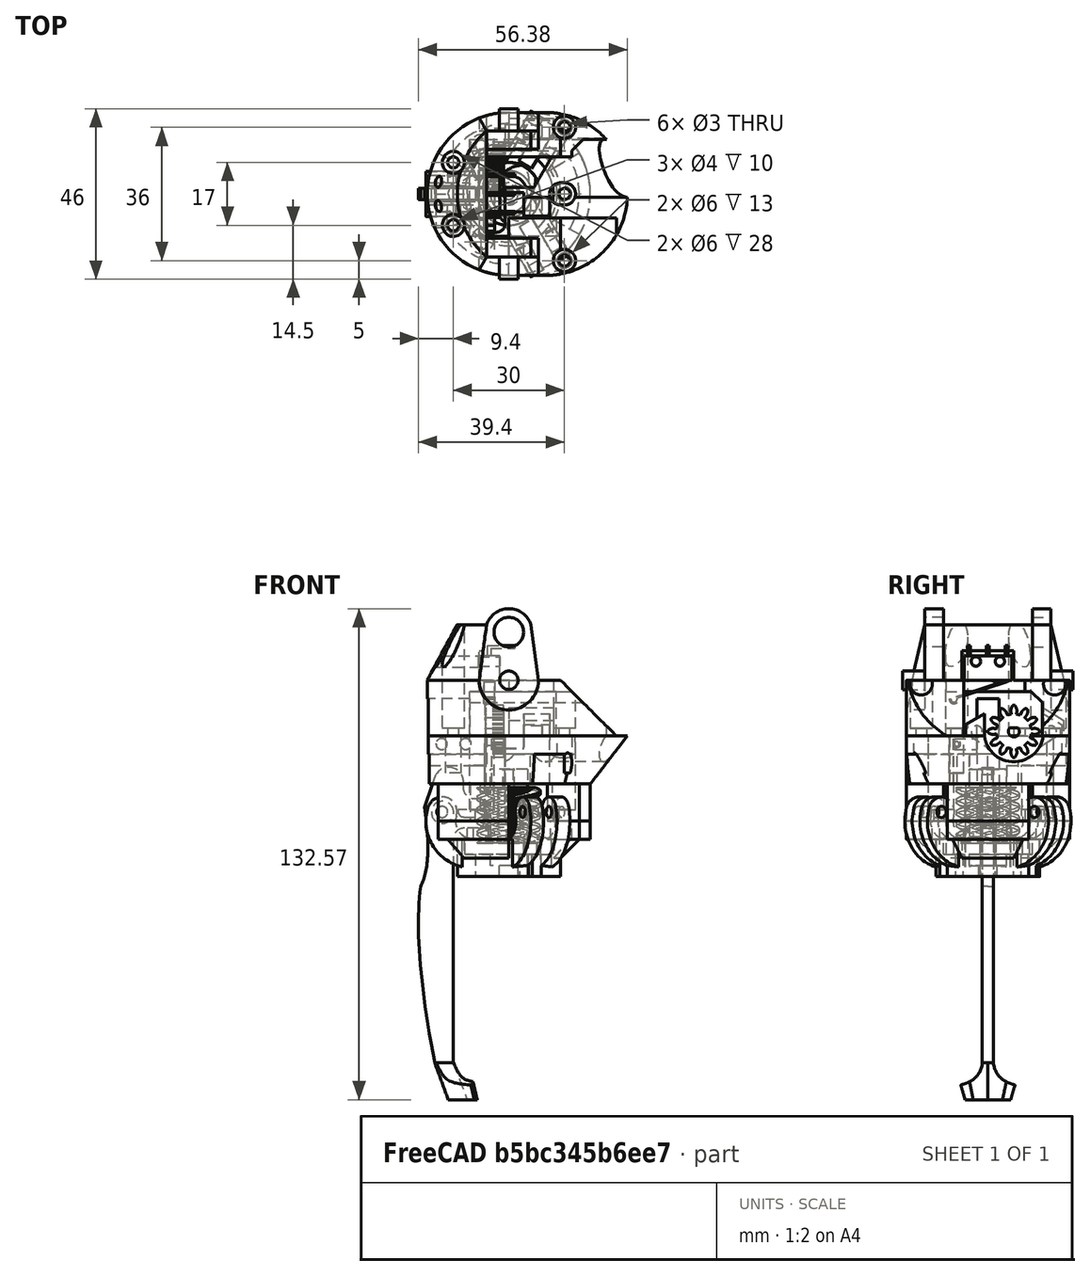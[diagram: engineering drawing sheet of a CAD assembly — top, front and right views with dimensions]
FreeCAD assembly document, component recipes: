
FREECAD ASSEMBLY — COMPONENT RECIPES ("GripperHolder")

This assembly document has 11 components, labeled P0..P10 below (a component is one placed body or linked part). 6 of them carry a construction recipe — the FreeCAD feature program that regenerates the part from scratch, quoted from this document or its linked companion documents; the rest are supplied as boundary geometry only. No exploded tour is included for this assembly.
COMPONENT P0 — recipe-attached ("GripperFinger", modeled in this document).
Construction recipe (the document's own serialized feature program — sketch geometry with constraints, then the solid features built on it; lengths are millimeters unless a unit is written):

FEATURE [Sketcher::SketchObject] Sketch014
  ArcFitTolerance = 1e-06
  AttachmentSupport = -> [XZ_Plane002]
  FullyConstrained = false
  MakeInternals = false
  MapMode = 5
  Placement = pos=(0,0,0) rot=(1,0,0;1.5708rad)
  sketch-geometry (24):
    g0: Circle [constr] CenterX=-20.7594 CenterY=-8.82234 CenterZ=0 NormalX=0 NormalY=0 NormalZ=1 AngleXU=0 Radius=1
    g1: Circle [constr] CenterX=-18.5613 CenterY=-24.1579 CenterZ=0 NormalX=0 NormalY=0 NormalZ=1 AngleXU=0 Radius=1
    g2: Circle [constr] CenterX=-21.8082 CenterY=-30.1322 CenterZ=0 NormalX=0 NormalY=0 NormalZ=1 AngleXU=0 Radius=1
    g3: BSplineCurve PolesCount=3 KnotsCount=2 Degree=2 IsPeriodic=0
    g4: GeomPoint [constr] X=-20.7594 Y=-8.82234 Z=0
    g5: GeomPoint [constr] X=-21.8082 Y=-30.1322 Z=0
    g6: Circle [constr] CenterX=-21.8082 CenterY=-30.1322 CenterZ=0 NormalX=0 NormalY=0 NormalZ=1 AngleXU=0 Radius=1
    g7: Circle [constr] CenterX=-24.0161 CenterY=-46.7563 CenterZ=0 NormalX=0 NormalY=0 NormalZ=1 AngleXU=0 Radius=1
    g8: Circle [constr] CenterX=-18 CenterY=-77.753 CenterZ=0 NormalX=0 NormalY=0 NormalZ=1 AngleXU=0 Radius=1
    g9: BSplineCurve PolesCount=3 KnotsCount=2 Degree=2 IsPeriodic=0
    g10: GeomPoint [constr] X=-21.8082 Y=-30.1322 Z=0
    g11: GeomPoint [constr] X=-18 Y=-77.753 Z=0
    g12: LineSegment StartX=-18 StartY=-77.753 StartZ=0 EndX=-13 EndY=-77.753 EndZ=0
    g13: LineSegment StartX=-20.7594 StartY=-8.82234 StartZ=0 EndX=-17.7673 EndY=-0.0858362 EndZ=0
    g14: ArcOfCircle CenterX=-14.2357 CenterY=-1.99234 CenterZ=0 NormalX=0 NormalY=0 NormalZ=1 AngleXU=0 Radius=4.01341 StartAngle=5.91393 EndAngle=8.92978
    g15: LineSegment StartX=-11.4259 StartY=-6.40926 StartZ=0 EndX=-10.4928 EndY=-3.44087 EndZ=0
    g16: LineSegment StartX=-13 StartY=-14.4093 StartZ=0 EndX=-13 EndY=-77.753 EndZ=0
    g17: LineSegment StartX=-11.4259 StartY=-6.40926 StartZ=0 EndX=-4.71716 EndY=-6.40926 EndZ=0
    g18: LineSegment StartX=-4.71716 StartY=-6.40926 StartZ=0 EndX=-4.71716 EndY=-9.40926 EndZ=0
    g19: LineSegment StartX=-4.71716 StartY=-9.40926 StartZ=0 EndX=-11.7172 EndY=-9.40926 EndZ=0
    g20: LineSegment StartX=-11.7172 StartY=-9.40926 StartZ=0 EndX=-11.7172 EndY=-11.4093 EndZ=0
    g21: LineSegment StartX=-11.7172 StartY=-11.4093 StartZ=0 EndX=-4.71716 EndY=-11.4093 EndZ=0
    g22: LineSegment StartX=-4.71716 StartY=-11.4093 StartZ=0 EndX=-4.71716 EndY=-14.4093 EndZ=0
    g23: LineSegment StartX=-4.71716 StartY=-14.4093 StartZ=0 EndX=-13 EndY=-14.4093 EndZ=0
  constraints (45):
    c: Weight(g0) = 1
    c: Equal(g0,g1)
    c: Equal(g0,g2)
    c: InternalAlignment(g0,g3)
    c: InternalAlignment(g1,g3)
    c: InternalAlignment(g2,g3)
    c: InternalAlignment(g4,g3)
    c: InternalAlignment(g5,g3)
    c: Weight(g6) = 1
    c: Equal(g6,g7)
    c: Equal(g6,g8)
    c: InternalAlignment(g6,g9)
    c: InternalAlignment(g7,g9)
    c: InternalAlignment(g8,g9)
    c: InternalAlignment(g10,g9)
    c: InternalAlignment(g11,g9)
    c: Coincident(g2,g6)
    c: Horizontal(g12,g8)
    c: Coincident(g12,g9)
    c: DistanceX(g12,g12) = 5
    c: Coincident(g13,g3)
    c: Coincident(g14,g13)
    c: Horizontal(g17)
    c: Coincident(g17,g18)
    c: Vertical(g18)
    c: Coincident(g18,g19)
    c: Horizontal(g19)
    c: Coincident(g19,g20)
    c: Vertical(g20)
    c: Coincident(g20,g21)
    c: Horizontal(g21)
    c: Coincident(g21,g22)
    c: Vertical(g22)
    c: Distance(g18,g18) = 3
    c: DistanceY(g22,g22) = 3
    c: DistanceY(g20,g20) = 2
    c: Vertical(g16)
    c: Coincident(g15,g17)
    c: Horizontal(g23)
    c: Coincident(g23,g22)
    c: Coincident(g16,g23)
    c: Vertical(g19,g21)
    c: Coincident(g14,g15)
    c: Coincident(g12,g16)
    c: DistanceX(g19,g19) = 7
FEATURE [PartDesign::Pad] Pad003
  Direction = (0,-1,2e-16)
  Length = 1.5
  Length2 = 10
  Placement = pos=(0,0,0) rot=(1,0,0;1.5708rad)
  Profile = -> Sketch014
  ReferenceAxis = -> Sketch014 [N_Axis]
  Refine = true
  Suppressed = false
  Type = 0
FEATURE [Sketcher::SketchObject] Sketch015
  ArcFitTolerance = 1e-06
  AttachmentSupport = -> [XZ_Plane002]
  FullyConstrained = false
  MakeInternals = false
  MapMode = 5
  Placement = pos=(0,0,0) rot=(1,0,0;1.5708rad)
  sketch-geometry (1):
    g0: Circle CenterX=-15.9022 CenterY=-10.1693 CenterZ=0 NormalX=0 NormalY=0 NormalZ=1 AngleXU=0 Radius=3
  constraints (1):
    c: Diameter(g0) = 6
FEATURE [PartDesign::Pocket] Pocket010
  BaseFeature = -> Pad003
  Direction = (0,1,-2e-16)
  Length = 5
  Length2 = 5
  Placement = pos=(0,0,0) rot=(1,0,0;1.5708rad)
  Profile = -> Sketch015
  ReferenceAxis = -> Sketch015 [N_Axis]
  Refine = true
  Reversed = true
  Suppressed = false
  Type = 0
FEATURE [Sketcher::SketchObject] Sketch016
  ArcFitTolerance = 1e-06
  AttachmentSupport = -> [Pocket010]
  FullyConstrained = false
  MakeInternals = false
  MapMode = 5
  Placement = pos=(0,-3.42e-14,-77.753) rot=(1,0,0;3.14159rad)
  sketch-geometry (10):
    g0: Circle [constr] CenterX=-13 CenterY=0 CenterZ=0 NormalX=0 NormalY=0 NormalZ=1 AngleXU=0 Radius=1
    g1: Circle [constr] CenterX=-13.004 CenterY=4.51884 CenterZ=0 NormalX=0 NormalY=0 NormalZ=1 AngleXU=0 Radius=1
    g2: Circle [constr] CenterX=-8.86046 CenterY=6.03618 CenterZ=0 NormalX=0 NormalY=0 NormalZ=1 AngleXU=0 Radius=1
    g3: BSplineCurve PolesCount=3 KnotsCount=2 Degree=2 IsPeriodic=0
    g4: Circle [constr] CenterX=-18 CenterY=0 CenterZ=0 NormalX=0 NormalY=0 NormalZ=1 AngleXU=0 Radius=1
    g5: Circle [constr] CenterX=-16.3304 CenterY=6.85321 CenterZ=0 NormalX=0 NormalY=0 NormalZ=1 AngleXU=0 Radius=1
    g6: Circle [constr] CenterX=-9.56077 CenterY=9.07086 CenterZ=0 NormalX=0 NormalY=0 NormalZ=1 AngleXU=0 Radius=1
    g7: BSplineCurve PolesCount=3 KnotsCount=2 Degree=2 IsPeriodic=0
    g8: LineSegment StartX=-9.56077 StartY=9.07086 StartZ=0 EndX=-8.86046 EndY=6.03618 EndZ=0
    g9: LineSegment StartX=-13 StartY=0 StartZ=0 EndX=-18 EndY=0 EndZ=0
  constraints (16):
    c: Weight(g0) = 1
    c: Equal(g0,g1)
    c: Equal(g0,g2)
    c: InternalAlignment(g0,g3)
    c: InternalAlignment(g1,g3)
    c: InternalAlignment(g2,g3)
    c: Weight(g4) = 1
    c: Equal(g4,g5)
    c: Equal(g4,g6)
    c: InternalAlignment(g4,g7)
    c: InternalAlignment(g5,g7)
    c: InternalAlignment(g6,g7)
    c: Coincident(g8,g7)
    c: Coincident(g8,g3)
    c: Coincident(g9,g7)
    c: Coincident(g9,g3)
FEATURE [Sketcher::SketchObject] Sketch017
  ArcFitTolerance = 1e-06
  AttachmentOffset = pos=(0,0,10) rot=(0,0,1;0rad)
  AttachmentSupport = -> [Pocket010]
  FullyConstrained = false
  MakeInternals = false
  MapMode = 5
  Placement = pos=(0,-3.42e-14,-87.753) rot=(1,0,0;3.14159rad)
  sketch-geometry (8):
    g0: Circle [constr] CenterX=-13.474 CenterY=5.13044 CenterZ=0 NormalX=0 NormalY=0 NormalZ=1 AngleXU=0 Radius=1
    g1: Circle [constr] CenterX=-7.36415 CenterY=6.15312 CenterZ=0 NormalX=0 NormalY=0 NormalZ=1 AngleXU=0 Radius=1
    g2: BSplineCurve PolesCount=3 KnotsCount=2 Degree=2 IsPeriodic=0
    g3: Circle [constr] CenterX=-9.38329 CenterY=2.79664 CenterZ=0 NormalX=0 NormalY=0 NormalZ=1 AngleXU=0 Radius=1
    g4: Circle [constr] CenterX=-6.52503 CenterY=3.95043 CenterZ=0 NormalX=0 NormalY=0 NormalZ=1 AngleXU=0 Radius=1
    g5: BSplineCurve PolesCount=3 KnotsCount=2 Degree=2 IsPeriodic=0
    g6: LineSegment StartX=-7.36415 StartY=6.15312 StartZ=0 EndX=-6.52503 EndY=3.95043 EndZ=0
    g7: LineSegment StartX=-14.3465 StartY=0 StartZ=0 EndX=-9.25279 EndY=0 EndZ=0
  constraints (10):
    c: InternalAlignment(g0,g2)
    c: InternalAlignment(g1,g2)
    c: InternalAlignment(g3,g5)
    c: InternalAlignment(g4,g5)
    c: Coincident(g6,g2)
    c: Coincident(g6,g5)
    c: Coincident(g7,g2)
    c: Horizontal(g7)
    c: Coincident(g5,g7)
    c: Horizontal(g5,g-1)
FEATURE [PartDesign::AdditiveLoft] AdditiveLoft002
  BaseFeature = -> Pocket010
  Closed = true
  Placement = pos=(0,0,0) rot=(1,0,0;1.5708rad)
  Profile = -> Sketch016
  Refine = true
  Ruled = true
  Sections = -> [Sketch017]
  Suppressed = false
FEATURE [Sketcher::SketchObject] Sketch018
  ArcFitTolerance = 1e-06
  AttachmentSupport = -> [YZ_Plane002]
  ExternalGeometry = -> [AdditiveLoft002]
  FullyConstrained = false
  MakeInternals = false
  MapMode = 5
  Placement = pos=(0,0,0) rot=(0.57735,0.57735,0.57735;2.0944rad)
  sketch-geometry (9):
    g0: Circle [constr] CenterX=-25.4284 CenterY=-84.2513 CenterZ=0 NormalX=0 NormalY=0 NormalZ=1 AngleXU=0 Radius=1
    g1: Circle [constr] CenterX=-2.16974 CenterY=-84.4568 CenterZ=0 NormalX=0 NormalY=0 NormalZ=1 AngleXU=0 Radius=1
    g2: Circle [constr] CenterX=-1.5 CenterY=-77.753 CenterZ=0 NormalX=0 NormalY=0 NormalZ=1 AngleXU=0 Radius=1
    g3: BSplineCurve PolesCount=3 KnotsCount=2 Degree=2 IsPeriodic=0
    g4: GeomPoint [constr] X=-12.8183 Y=-84.2513 Z=0
    g5: GeomPoint [constr] X=-1.5 Y=-77.753 Z=0
    g6: LineSegment StartX=-14.8386 StartY=-84.2513 StartZ=0 EndX=-14.8386 EndY=-77.2874 EndZ=0
    g7: LineSegment StartX=-14.8386 StartY=-77.2874 StartZ=0 EndX=-1.5 EndY=-77.753 EndZ=0
    g8: LineSegment StartX=-14.8386 StartY=-84.2513 StartZ=0 EndX=-12.8183 EndY=-84.2513 EndZ=0
  constraints (14):
    c: Weight(g0) = 1
    c: Equal(g0,g1)
    c: Equal(g0,g2)
    c: InternalAlignment(g1,g3)
    c: InternalAlignment(g2,g3)
    c: InternalAlignment(g4,g3)
    c: InternalAlignment(g5,g3)
    c: Vertical(g6)
    c: Coincident(g6,g7)
    c: Coincident(g7,g3)
    c: Coincident(g6,g8)
    c: Coincident(g8,g3)
    c: Horizontal(g8)
    c: Horizontal(g3,g0)
FEATURE [PartDesign::Pocket] Pocket005
  BaseFeature = -> AdditiveLoft002
  Direction = (-1,0,0)
  Length = 5
  Length2 = 5
  Placement = pos=(0,0,0) rot=(1,0,0;1.5708rad)
  Profile = -> Sketch018
  ReferenceAxis = -> Sketch018 [N_Axis]
  Refine = true
  Suppressed = false
  Type = 1
FEATURE [PartDesign::Mirrored] Mirrored001
  BaseFeature = -> Pocket005
  MirrorPlane = -> XZ_Plane002
  Placement = pos=(0,0,0) rot=(1,0,0;1.5708rad)
  Refine = true
  Suppressed = false
  TransformMode = 1
FEATURE [PartDesign::Fillet] Fillet
  Base = -> Mirrored001 [Edge70,Edge68]
  BaseFeature = -> Mirrored001
  Placement = pos=(0,0,0) rot=(1,0,0;1.5708rad)
  Radius = 3
  Refine = true
  SupportTransform = false
  Suppressed = false
  UseAllEdges = false
FEATURE [PartDesign::Fillet] Fillet001
  Base = -> Fillet [Edge26,Edge49,Edge37]
  BaseFeature = -> Fillet
  Placement = pos=(0,0,0) rot=(1,0,0;1.5708rad)
  Radius = 1.5
  Refine = true
  SupportTransform = false
  Suppressed = false
  UseAllEdges = false
FEATURE [PartDesign::Body] Body002  label="GripperFinger"
  AllowCompound = false
  Group = -> [Sketch014,Pad003,Pocket010,Sketch015,Sketch016,Sketch017,AdditiveLoft002,Sketch018,Pocket005,Mirrored001,Fillet,Fillet001]
  Origin = -> Origin002
  Placement = pos=(-2,0,-10.5) rot=(0,0,1;0rad)
  Tip = -> Fillet001
COMPONENT P1 — recipe-attached ("GripperHolderBottom", modeled in this document).
Construction recipe (the document's own serialized feature program — sketch geometry with constraints, then the solid features built on it; lengths are millimeters unless a unit is written):

FEATURE [Sketcher::SketchObject] Sketch024
  ArcFitTolerance = 1e-06
  AttachmentSupport = -> [XY_Plane004]
  FullyConstrained = true
  MakeInternals = false
  MapMode = 5
  sketch-geometry (2):
    g0: Circle CenterX=0 CenterY=0 CenterZ=0 NormalX=0 NormalY=0 NormalZ=1 AngleXU=0 Radius=2.5
    g1: Circle CenterX=0 CenterY=0 CenterZ=0 NormalX=0 NormalY=0 NormalZ=1 AngleXU=0 Radius=14
  constraints (4):
    c: Coincident(g0,g-1)
    c: Coincident(g1,g0)
    c: Diameter(g1) = 28
    c: Diameter(g0) = 5
FEATURE [PartDesign::Pad] Pad006
  Direction = (0,0,1)
  Length = 10
  Length2 = 10
  Profile = -> Sketch024
  ReferenceAxis = -> Sketch024 [N_Axis]
  Refine = true
  Reversed = true
  Suppressed = false
  Type = 0
FEATURE [Sketcher::SketchObject] Sketch025
  ArcFitTolerance = 1e-06
  AttachmentOffset = pos=(0,0,2.1) rot=(0,0,1;0rad)
  AttachmentSupport = -> [XZ_Plane004]
  FullyConstrained = false
  MakeInternals = false
  MapMode = 5
  Placement = pos=(0,-2.1,5e-16) rot=(1,0,0;1.5708rad)
  sketch-geometry (4):
    g0: ArcOfCircle CenterX=-9.71119 CenterY=4.94669 CenterZ=0 NormalX=0 NormalY=0 NormalZ=1 AngleXU=0 Radius=12.6732 StartAngle=2.84277 EndAngle=4.68735
    g1: ArcOfCircle CenterX=-18 CenterY=7.5 CenterZ=0 NormalX=0 NormalY=0 NormalZ=1 AngleXU=0 Radius=4 StartAngle=5.98437 EndAngle=9.12596
    g2: ArcOfCircle CenterX=-9.92832 CenterY=-3.72375 CenterZ=0 NormalX=0 NormalY=0 NormalZ=1 AngleXU=0 Radius=4 StartAngle=4.68735 EndAngle=7.82894
    g3: ArcOfCircle CenterX=-9.71119 CenterY=4.94669 CenterZ=0 NormalX=0 NormalY=0 NormalZ=1 AngleXU=0 Radius=4.67316 StartAngle=2.84277 EndAngle=4.68735
  constraints (8):
    c: Coincident(g0,g3)
    c: Tangent(g3,g2) = 1.5708
    c: Tangent(g3,g1) = 1.5708
    c: Tangent(g0,g2) = -1.5708
    c: Tangent(g0,g1) = -1.5708
    c: Radius(g1) = 4
    c: DistanceY(g-1,g1) = 7.5
    c: DistanceX(g1,g-1) = 18
FEATURE [PartDesign::Pad] Pad007
  BaseFeature = -> Pad006
  Direction = (0,-1,2e-16)
  Length = 4
  Length2 = 10
  Profile = -> Sketch025
  ReferenceAxis = -> Sketch025 [N_Axis]
  Refine = true
  Suppressed = false
  Type = 0
FEATURE [Sketcher::SketchObject] Sketch026
  ArcFitTolerance = 1e-06
  AttachmentSupport = -> [Pad007]
  FullyConstrained = false
  MakeInternals = false
  MapMode = 5
  Placement = pos=(0,-6.1,1.3e-15) rot=(1,0,0;1.5708rad)
  sketch-geometry (1):
    g0: Circle CenterX=-17.9735 CenterY=7.44527 CenterZ=0 NormalX=0 NormalY=0 NormalZ=1 AngleXU=0 Radius=1.5
  constraints (1):
    c: Diameter(g0) = 3
FEATURE [PartDesign::Pocket] Pocket011
  BaseFeature = -> Pad007
  Direction = (0,1,-2e-16)
  Length = 5
  Length2 = 5
  Profile = -> Sketch026
  ReferenceAxis = -> Sketch026 [N_Axis]
  Refine = true
  Suppressed = false
  Type = 0
FEATURE [PartDesign::Mirrored] Mirrored003
  BaseFeature = -> Pocket011
  MirrorPlane = -> XZ_Plane004
  Originals = -> [Pocket011]
  Refine = true
  Suppressed = false
  TransformMode = 1
FEATURE [PartDesign::PolarPattern] PolarPattern001
  Angle = 360
  Axis = -> Z_Axis004
  BaseFeature = -> Mirrored003
  Mode = 0
  Occurrences = 3
  Offset = 120
  Originals = -> [Mirrored003]
  Refine = true
  Suppressed = false
  TransformMode = 1
FEATURE [Sketcher::SketchObject] Sketch027
  ArcFitTolerance = 1e-06
  AttachmentSupport = -> [PolarPattern001]
  FullyConstrained = false
  MakeInternals = false
  MapMode = 5
  sketch-geometry (4):
    g0: ArcOfCircle CenterX=0 CenterY=0 CenterZ=0 NormalX=0 NormalY=0 NormalZ=1 AngleXU=0 Radius=22 StartAngle=1.57083 EndAngle=2.61805
    g1: LineSegment StartX=-19.0531 StartY=10.999 StartZ=0 EndX=-11.2589 EndY=6.49899 EndZ=0
    g2: ArcOfCircle CenterX=0 CenterY=0 CenterZ=0 NormalX=0 NormalY=0 NormalZ=1 AngleXU=0 Radius=13 StartAngle=1.57085 EndAngle=2.61808
    g3: LineSegment StartX=-0.000708834 StartY=22 StartZ=0 EndX=-0.000708834 EndY=13 EndZ=0
  constraints (10):
    c: Coincident(g0,g-1)
    c: Coincident(g1,g0)
    c: Coincident(g1,g2)
    c: Coincident(g3,g0)
    c: Coincident(g3,g2)
    c: Angle(g1,g-1) = 0.523599
    c: Vertical(g3)
    c: Coincident(g0,g2)
    c: Radius(g0) = 22
    c: Radius(g2) = 13
FEATURE [PartDesign::Pad] Pad008
  BaseFeature = -> PolarPattern001
  Direction = (0,0,1)
  Length = 5
  Length2 = 10
  Profile = -> Sketch027
  ReferenceAxis = -> Sketch027 [N_Axis]
  Refine = true
  Suppressed = false
  Type = 0
FEATURE [PartDesign::PolarPattern] PolarPattern002
  Angle = 360
  Axis = -> Sketch027 [N_Axis]
  BaseFeature = -> Pad008
  Mode = 0
  Occurrences = 3
  Offset = 120
  Originals = -> [Pad008]
  Refine = true
  Suppressed = false
  TransformMode = 0
FEATURE [Sketcher::SketchObject] Sketch031
  ArcFitTolerance = 1e-06
  AttachmentSupport = -> [YZ_Plane004]
  FullyConstrained = true
  MakeInternals = false
  MapMode = 5
  Placement = pos=(0,0,0) rot=(0.57735,0.57735,0.57735;2.0944rad)
  sketch-geometry (4):
    g0: LineSegment StartX=3 StartY=22 StartZ=0 EndX=-3 EndY=22 EndZ=0
    g1: LineSegment StartX=-3 StartY=22 StartZ=0 EndX=-3 EndY=15 EndZ=0
    g2: LineSegment StartX=-3 StartY=15 StartZ=0 EndX=3 EndY=15 EndZ=0
    g3: LineSegment StartX=3 StartY=15 StartZ=0 EndX=3 EndY=22 EndZ=0
  constraints (12):
    c: Coincident(g0,g1)
    c: Coincident(g1,g2)
    c: Coincident(g2,g3)
    c: Coincident(g3,g0)
    c: Horizontal(g0)
    c: Horizontal(g2)
    c: Vertical(g1)
    c: Vertical(g3)
    c: Distance(g-1,g2) = 15
    c: Distance(g-2,g1) = 3
    c: Distance(g-2,g3) = 3
    c: DistanceY(g3,g3) = 7
FEATURE [PartDesign::Pocket] Pocket013
  BaseFeature = -> PolarPattern002
  Direction = (-1,0,0)
  Length = 5
  Length2 = 5
  Profile = -> Sketch031
  ReferenceAxis = -> Sketch031 [N_Axis]
  Refine = true
  Suppressed = false
  Type = 1
FEATURE [PartDesign::PolarPattern] PolarPattern005
  Angle = 360
  Axis = -> Z_Axis004
  BaseFeature = -> Pocket013
  Mode = 0
  Occurrences = 3
  Offset = 120
  Originals = -> [Pocket013]
  Refine = true
  Suppressed = false
  TransformMode = 0
FEATURE [PartDesign::Chamfer] Chamfer
  Angle = 45
  Base = -> PolarPattern005 [Edge60,Edge61,Edge67,Edge68,Edge53,Edge48]
  BaseFeature = -> PolarPattern005
  ChamferType = 0
  FlipDirection = false
  Refine = true
  Size = 5
  Size2 = 7
  SupportTransform = false
  Suppressed = false
  UseAllEdges = false
FEATURE [Sketcher::SketchObject] Sketch048
  ArcFitTolerance = 1e-06
  AttachmentSupport = -> [Chamfer]
  FullyConstrained = true
  MakeInternals = false
  MapMode = 5
  Placement = pos=(0,0,5) rot=(0,0,1;0rad)
  sketch-geometry (1):
    g0: Circle CenterX=15 CenterY=0 CenterZ=0 NormalX=0 NormalY=0 NormalZ=1 AngleXU=0 Radius=2
  constraints (3):
    c: PointOnObject(g0,g-1)
    c: Diameter(g0) = 4
    c: DistanceX(g-1,g0) = 15
FEATURE [PartDesign::Pocket] Pocket020
  BaseFeature = -> Chamfer
  Direction = (0,0,-1)
  Length = 5
  Length2 = 5
  Profile = -> Sketch048
  ReferenceAxis = -> Sketch048 [N_Axis]
  Refine = true
  Suppressed = false
  Type = 0
FEATURE [PartDesign::PolarPattern] PolarPattern009
  Angle = 360
  Axis = -> Sketch048 [N_Axis]
  BaseFeature = -> Pocket020
  Mode = 0
  Occurrences = 3
  Offset = 120
  Originals = -> [Pocket020]
  Refine = true
  Suppressed = false
  TransformMode = 0
FEATURE [Sketcher::SketchObject] Sketch059
  ArcFitTolerance = 1e-06
  AttachmentSupport = -> [PolarPattern009]
  FullyConstrained = false
  MakeInternals = false
  MapMode = 5
  Placement = pos=(0,-2.1,5e-16) rot=(0,0.707107,0.707107;3.14159rad)
  sketch-geometry (4):
    g0: ArcOfCircle CenterX=18 CenterY=7.5 CenterZ=0 NormalX=0 NormalY=0 NormalZ=1 AngleXU=0 Radius=13 StartAngle=5.14611 EndAngle=10.2309
    g1: LineSegment StartX=9 StartY=-1.88083 StartZ=0 EndX=9 EndY=-14.3112 EndZ=0
    g2: LineSegment StartX=9 StartY=-14.3112 StartZ=0 EndX=23.4632 EndY=-14.3112 EndZ=0
    g3: LineSegment StartX=23.4632 StartY=-14.3112 StartZ=0 EndX=23.4632 EndY=-4.29632 EndZ=0
  constraints (11):
    c: DistanceY(g-1,g0) = 7.5
    c: DistanceX(g-1,g0) = 18
    c: Diameter(g0) = 26
    c: Coincident(g1,g2)
    c: Coincident(g2,g3)
    c: Vertical(g1)
    c: Vertical(g3)
    c: Horizontal(g2)
    c: Distance(g-2,g1) = 9
    c: Coincident(g0,g1)
    c: Coincident(g0,g3)
FEATURE [PartDesign::Pocket] Pocket027
  BaseFeature = -> PolarPattern009
  Direction = (0,-1,2e-16)
  Length = 4
  Length2 = 5
  Profile = -> Sketch059
  ReferenceAxis = -> Sketch059 [N_Axis]
  Refine = true
  Reversed = true
  Suppressed = false
  Type = 0
FEATURE [PartDesign::PolarPattern] PolarPattern010
  Angle = 360
  Axis = -> Z_Axis004
  BaseFeature = -> Pocket027
  Mode = 0
  Occurrences = 3
  Offset = 120
  Originals = -> [Pocket027]
  Refine = true
  Suppressed = false
  TransformMode = 0
FEATURE [Sketcher::SketchObject] Sketch060
  ArcFitTolerance = 1e-06
  AttachmentOffset = pos=(0,0,1) rot=(0,0,1;0rad)
  AttachmentSupport = -> [PolarPattern010]
  FullyConstrained = true
  MakeInternals = false
  MapMode = 5
  Placement = pos=(0,0,1) rot=(0,0,1;0rad)
  sketch-geometry (1):
    g0: Circle CenterX=0 CenterY=0 CenterZ=0 NormalX=0 NormalY=0 NormalZ=1 AngleXU=0 Radius=12
  constraints (2):
    c: Coincident(g0,g-1)
    c: Diameter(g0) = 24
FEATURE [PartDesign::Pocket] Pocket028
  BaseFeature = -> PolarPattern010
  Direction = (0,0,-1)
  Length = 5
  Length2 = 5
  Profile = -> Sketch060
  ReferenceAxis = -> Sketch060 [N_Axis]
  Refine = true
  Suppressed = false
  Type = 0
FEATURE [Sketcher::SketchObject] Sketch116
  ArcFitTolerance = 1e-06
  AttachmentSupport = -> [Pocket028]
  FullyConstrained = true
  MakeInternals = false
  MapMode = 5
  Placement = pos=(0,0,-4) rot=(0,0,1;0rad)
  sketch-geometry (1):
    g0: Circle CenterX=0 CenterY=0 CenterZ=0 NormalX=0 NormalY=0 NormalZ=1 AngleXU=0 Radius=5
  constraints (2):
    c: Diameter(g0) = 10
    c: Coincident(g0,g-1)
FEATURE [PartDesign::Pocket] Pocket076
  BaseFeature = -> Pocket028
  Direction = (0,0,-1)
  Length = 3
  Length2 = 5
  Profile = -> Sketch116
  ReferenceAxis = -> Sketch116 [N_Axis]
  Refine = true
  Suppressed = false
  Type = 0
FEATURE [PartDesign::Body] Body004  label="GripperHolderBottom"
  AllowCompound = false
  Group = -> [Sketch024,Pad006,Sketch025,Pad007,Pocket011,Mirrored003,Sketch026,PolarPattern001,Sketch027,Pad008,PolarPattern002,Sketch031,Pocket013,PolarPattern005,Chamfer,Sketch048,Pocket020,PolarPattern009,Sketch059,Pocket027,PolarPattern010,Sketch060,Pocket028,Sketch116,Pocket076]
  Origin = -> Origin004
  Placement = pos=(0,0,-28) rot=(0,0,1;0rad)
  Tip = -> Pocket076
COMPONENT P2 — recipe-attached ("WormGear003", modeled in this document).
Construction recipe (the document's own serialized feature program — sketch geometry with constraints, then the solid features built on it; lengths are millimeters unless a unit is written):

FEATURE [PartDesign::FeaturePython] WormGear001  # WARN: FeaturePython — macro-defined, semantics opaque (R4)
  AttacherType = Attacher::AttachEngine3D
  Suppressed = false
  beta = 11.3099
  clearance = 0.25
  diameter = 15
  head = 0
  height = 20
  module = 1
  num_teeth = 3
  pressure_angle = 20
  reverse_pitch = false
  version = 1.3.0
FEATURE [Sketcher::SketchObject] Sketch080
  ArcFitTolerance = 1e-06
  AttachmentSupport = -> [WormGear001]
  FullyConstrained = true
  MakeInternals = false
  MapMode = 5
  Placement = pos=(-0.000288442,-0.000277997,19.9998) rot=(0.693951,-0.720023,-5e-06;2e-05rad)
  sketch-geometry (2):
    g0: ArcOfCircle CenterX=0 CenterY=0 CenterZ=0 NormalX=0 NormalY=0 NormalZ=1 AngleXU=0 Radius=1.5 StartAngle=2.41186 EndAngle=7.01291
    g1: LineSegment StartX=-1.11803 StartY=1 StartZ=0 EndX=1.11803 EndY=1 EndZ=0
  constraints (6):
    c: Diameter(g0) = 3
    c: Coincident(g0,g-1)
    c: Horizontal(g1)
    c: Distance(g0,g1) = 1
    c: Coincident(g0,g1)
    c: Coincident(g1,g0)
FEATURE [PartDesign::Pocket] Pocket044
  BaseFeature = -> WormGear001
  Direction = (1.44222e-05,1.39e-05,-1)
  Length = 10
  Length2 = 5
  Profile = -> Sketch080
  ReferenceAxis = -> Sketch080 [N_Axis]
  Refine = true
  Suppressed = false
  Type = 0
FEATURE [Sketcher::SketchObject] Sketch082
  ArcFitTolerance = 1e-06
  AttachmentSupport = -> [Pocket044]
  FullyConstrained = true
  MakeInternals = false
  MapMode = 5
  Placement = pos=(0,0,0) rot=(1,0,0;3.14159rad)
  sketch-geometry (1):
    g0: Circle CenterX=0 CenterY=0 CenterZ=0 NormalX=0 NormalY=0 NormalZ=1 AngleXU=0 Radius=5
  constraints (2):
    c: Coincident(g0,g-1)
    c: Diameter(g0) = 10
FEATURE [PartDesign::Pocket] Pocket046
  BaseFeature = -> Pocket044
  Direction = (0,0,1)
  Length = 5
  Length2 = 5
  Profile = -> Sketch082
  ReferenceAxis = -> Sketch082 [N_Axis]
  Refine = true
  Suppressed = false
  Type = 0
FEATURE [Sketcher::SketchObject] Sketch083
  ArcFitTolerance = 1e-06
  AttachmentSupport = -> [Pocket046]
  FullyConstrained = true
  MakeInternals = false
  MapMode = 5
  Placement = pos=(0,0,5) rot=(1,0,0;3.14159rad)
  sketch-geometry (1):
    g0: Circle CenterX=0 CenterY=0 CenterZ=0 NormalX=0 NormalY=0 NormalZ=1 AngleXU=0 Radius=3
  constraints (2):
    c: Coincident(g0,g-1)
    c: Diameter(g0) = 6
FEATURE [PartDesign::Pocket] Pocket047
  BaseFeature = -> Pocket046
  Direction = (0,0,1)
  Length = 10
  Length2 = 5
  Profile = -> Sketch083
  ReferenceAxis = -> Sketch083 [N_Axis]
  Refine = true
  Suppressed = false
  Type = 0
FEATURE [Sketcher::SketchObject] Sketch084
  ArcFitTolerance = 1e-06
  AttachmentSupport = -> [Pocket047]
  FullyConstrained = true
  MakeInternals = false
  MapMode = 5
  Placement = pos=(-0.000288442,-0.000277997,19.9998) rot=(0.693951,-0.720023,-5e-06;2e-05rad)
  sketch-geometry (2):
    g0: Circle CenterX=0 CenterY=0 CenterZ=0 NormalX=0 NormalY=0 NormalZ=1 AngleXU=0 Radius=5
    g1: Circle CenterX=0 CenterY=0 CenterZ=0 NormalX=0 NormalY=0 NormalZ=1 AngleXU=0 Radius=10
  constraints (4):
    c: Diameter(g0) = 10
    c: Coincident(g0,g-1)
    c: Diameter(g1) = 20
    c: Coincident(g1,g0)
FEATURE [PartDesign::Pocket] Pocket048
  BaseFeature = -> Pocket047
  Direction = (1.44222e-05,1.39e-05,-1)
  Length = 5
  Length2 = 5
  Profile = -> Sketch084
  ReferenceAxis = -> Sketch084 [N_Axis]
  Refine = true
  Suppressed = false
  Type = 0
FEATURE [PartDesign::Body] Body010  label="WormGear003"
  AllowCompound = false
  Group = -> [WormGear001,Sketch080,Pocket044,Sketch082,Pocket046,Sketch083,Pocket047,Sketch084,Pocket048]
  Origin = -> Origin010
  Placement = pos=(0,0,-29) rot=(0,0,1;0rad)
  Tip = -> Pocket048
COMPONENT P3 — recipe-attached ("GearMotor", modeled in this document).
Construction recipe (the document's own serialized feature program — sketch geometry with constraints, then the solid features built on it; lengths are millimeters unless a unit is written):

FEATURE [PartDesign::FeaturePython] InvoluteGear  # WARN: FeaturePython — macro-defined, semantics opaque (R4)
  AttacherType = Attacher::AttachEngine3D
  Suppressed = false
  addendum_diameter = 14
  angular_backlash = 0
  axle_hole = false
  axle_holesize = 10
  backlash = 0
  clearance = 0.25
  double_helix = false
  head = 0
  head_fillet = 0
  height = 5
  helix_angle = 0
  module = 1
  num_teeth = 12
  numpoints = 20
  offset_hole = false
  offset_holeoffset = 10
  offset_holesize = 10
  pitch_diameter = 12
  pressure_angle = 20
  properties_from_tool = false
  reversed_backlash = false
  root_diameter = 9.5
  root_fillet = 0
  shift = 0
  simple = false
  transverse_pitch = 3.14159
  traverse_module = 1
  undercut = false
  version = 1.3.0
  expr: angular_backlash = backlash / pitch_diameter * 360 ° / pi
FEATURE [Sketcher::SketchObject] Sketch115
  ArcFitTolerance = 1e-06
  AttachmentSupport = -> [InvoluteGear]
  FullyConstrained = true
  MakeInternals = false
  MapMode = 5
  Placement = pos=(0,0,0) rot=(1,0,0;3.14159rad)
  sketch-geometry (2):
    g0: ArcOfCircle CenterX=0 CenterY=0 CenterZ=0 NormalX=0 NormalY=0 NormalZ=1 AngleXU=0 Radius=1.5 StartAngle=0.841069 EndAngle=5.44212
    g1: LineSegment StartX=1 StartY=1.11803 StartZ=0 EndX=1 EndY=-1.11803 EndZ=0
  constraints (6):
    c: Diameter(g0) = 3
    c: Coincident(g0,g-1)
    c: Vertical(g1)
    c: Distance(g-2,g1) = 1
    c: Coincident(g1,g0)
    c: Coincident(g1,g0)
FEATURE [PartDesign::Pocket] Pocket075
  BaseFeature = -> InvoluteGear
  Direction = (0,0,1)
  Length = 5
  Length2 = 5
  Profile = -> Sketch115
  ReferenceAxis = -> Sketch115 [N_Axis]
  Refine = true
  Suppressed = false
  Type = 0
FEATURE [PartDesign::Body] Body011  label="GearMotor"
  AllowCompound = false
  Group = -> [InvoluteGear,Sketch115,Pocket075]
  Origin = -> Origin011
  Placement = pos=(-1.4,7,1.2) rot=(0,1,0;4.71239rad)
  Tip = -> Pocket075
COMPONENT P4 — recipe-attached ("GripperHolderMiddle002", modeled in this document).
Construction recipe (the document's own serialized feature program — sketch geometry with constraints, then the solid features built on it; lengths are millimeters unless a unit is written):

FEATURE [Sketcher::SketchObject] Sketch092
  ArcFitTolerance = 1e-06
  AttachmentOffset = pos=(0,0,8) rot=(0,0,1;0rad)
  FullyConstrained = true
  MakeInternals = false
  MapMode = 5
  Placement = pos=(0,0,28) rot=(0,0,1;0rad)
  sketch-geometry (4):
    g0: ArcOfCircle CenterX=0 CenterY=0 CenterZ=0 NormalX=0 NormalY=0 NormalZ=1 AngleXU=0 Radius=22 StartAngle=1.5708 EndAngle=4.71239
    g1: ArcOfCircle CenterX=10 CenterY=9e-16 CenterZ=0 NormalX=0 NormalY=0 NormalZ=1 AngleXU=0 Radius=22 StartAngle=4.71239 EndAngle=7.85398
    g2: LineSegment StartX=-3.5e-15 StartY=22 StartZ=0 EndX=10 EndY=22 EndZ=0
    g3: LineSegment StartX=-4e-15 StartY=-22 StartZ=0 EndX=10 EndY=-22 EndZ=0
  constraints (9):
    c: Tangent(g0,g2) = 1.5708
    c: Tangent(g0,g3) = -1.5708
    c: Tangent(g1,g2) = 1.5708
    c: Tangent(g1,g3) = -1.5708
    c: Equal(g0,g1)
    c: Horizontal(g3)
    c: Coincident(g0,g-1)
    c: DistanceX(g-1,g1) = 10
    c: Radius(g0) = 22
FEATURE [Sketcher::SketchObject] Sketch093
  ArcFitTolerance = 1e-06
  FullyConstrained = true
  MakeInternals = false
  MapMode = 5
  Placement = pos=(0,0,15) rot=(0,0,1;0rad)
  sketch-geometry (1):
    g0: Circle CenterX=0 CenterY=0 CenterZ=0 NormalX=0 NormalY=0 NormalZ=1 AngleXU=0 Radius=22
  constraints (2):
    c: Coincident(g0,g-1)
    c: Diameter(g0) = 44
FEATURE [PartDesign::AdditiveLoft] AdditiveLoft007
  Closed = false
  Placement = pos=(0,0,28) rot=(0,0,1;0rad)
  Profile = -> Sketch092
  Refine = true
  Ruled = false
  Sections = -> [Sketch093]
  Suppressed = false
FEATURE [Sketcher::SketchObject] Sketch095
  ArcFitTolerance = 1e-06
  FullyConstrained = false
  MakeInternals = false
  MapMode = 5
  Placement = pos=(0,0,15) rot=(1,0,0;3.14159rad)
  sketch-geometry (4):
    g0: ArcOfCircle CenterX=0 CenterY=0 CenterZ=0 NormalX=0 NormalY=0 NormalZ=1 AngleXU=0 Radius=22 StartAngle=1.57083 EndAngle=2.618
    g1: LineSegment StartX=-19.0526 StartY=10.9999 StartZ=0 EndX=-10.3923 EndY=5.99993 EndZ=0
    g2: ArcOfCircle CenterX=0 CenterY=0 CenterZ=0 NormalX=0 NormalY=0 NormalZ=1 AngleXU=0 Radius=12 StartAngle=1.57086 EndAngle=2.618
    g3: LineSegment StartX=-0.000809479 StartY=22 StartZ=0 EndX=-0.000809479 EndY=12 EndZ=0
  constraints (10):
    c: Coincident(g0,g-1)
    c: Coincident(g1,g0)
    c: Coincident(g1,g2)
    c: Coincident(g3,g0)
    c: Coincident(g3,g2)
    c: Angle(g1,g-1) = 0.523599
    c: Vertical(g3)
    c: Coincident(g0,g2)
    c: Radius(g0) = 22
    c: Radius(g2) = 12
FEATURE [PartDesign::Pad] Pad013
  BaseFeature = -> AdditiveLoft007
  Direction = (0,0,-1)
  Length = 10
  Length2 = 10
  Placement = pos=(0,0,28) rot=(0,0,1;0rad)
  Profile = -> Sketch095
  ReferenceAxis = -> Sketch095 [N_Axis]
  Refine = true
  Suppressed = false
  Type = 0
FEATURE [PartDesign::PolarPattern] PolarPattern016
  Angle = 360
  Axis = -> Sketch095 [N_Axis]
  BaseFeature = -> Pad013
  Mode = 0
  Occurrences = 3
  Offset = 120
  Originals = -> [Pad013]
  Placement = pos=(0,0,28) rot=(0,0,1;0rad)
  Refine = true
  Suppressed = false
  TransformMode = 0
FEATURE [Sketcher::SketchObject] Sketch096
  ArcFitTolerance = 1e-06
  AttachmentSupport = -> [PolarPattern016]
  FullyConstrained = true
  MakeInternals = false
  MapMode = 5
  Placement = pos=(0,0,28) rot=(0,0,1;0rad)
  sketch-geometry (4):
    g0: ArcOfCircle CenterX=14 CenterY=0 CenterZ=0 NormalX=0 NormalY=0 NormalZ=1 AngleXU=0 Radius=3 StartAngle=1.5708 EndAngle=4.71239
    g1: ArcOfCircle CenterX=15 CenterY=1e-16 CenterZ=0 NormalX=0 NormalY=0 NormalZ=1 AngleXU=0 Radius=3 StartAngle=4.71239 EndAngle=7.85398
    g2: LineSegment StartX=14 StartY=3 StartZ=0 EndX=15 EndY=3 EndZ=0
    g3: LineSegment StartX=14 StartY=-3 StartZ=0 EndX=15 EndY=-3 EndZ=0
  constraints (10):
    c: Tangent(g0,g2) = 1.5708
    c: Tangent(g0,g3) = -1.5708
    c: Tangent(g1,g2) = 1.5708
    c: Tangent(g1,g3) = -1.5708
    c: Equal(g0,g1)
    c: Horizontal(g3)
    c: PointOnObject(g0,g-1)
    c: DistanceX(g-1,g1) = 15
    c: DistanceX(g0,g1) = 1
    c: Radius(g1) = 3
FEATURE [PartDesign::Pocket] Pocket057
  BaseFeature = -> PolarPattern016
  Direction = (0,0,-1)
  Length = 20
  Length2 = 5
  Placement = pos=(0,0,28) rot=(0,0,1;0rad)
  Profile = -> Sketch096
  ReferenceAxis = -> Sketch096 [N_Axis]
  Refine = true
  Suppressed = false
  Type = 0
FEATURE [PartDesign::PolarPattern] PolarPattern017
  Angle = 360
  Axis = -> Sketch096 [N_Axis]
  BaseFeature = -> Pocket057
  Mode = 0
  Occurrences = 3
  Offset = 120
  Originals = -> [Pocket057]
  Placement = pos=(0,0,28) rot=(0,0,1;0rad)
  Refine = true
  Suppressed = false
  TransformMode = 0
FEATURE [Sketcher::SketchObject] Sketch097
  ArcFitTolerance = 1e-06
  AttachmentSupport = -> [PolarPattern017]
  FullyConstrained = true
  MakeInternals = false
  MapMode = 5
  Placement = pos=(0,0,8) rot=(0,0,1;0rad)
  sketch-geometry (1):
    g0: Circle CenterX=15 CenterY=0 CenterZ=0 NormalX=0 NormalY=0 NormalZ=1 AngleXU=0 Radius=1.5
  constraints (3):
    c: PointOnObject(g0,g-1)
    c: Diameter(g0) = 3
    c: DistanceX(g-1,g0) = 15
FEATURE [PartDesign::Pocket] Pocket058
  BaseFeature = -> PolarPattern017
  Direction = (0,0,-1)
  Length = 5
  Length2 = 5
  Placement = pos=(0,0,28) rot=(0,0,1;0rad)
  Profile = -> Sketch097
  ReferenceAxis = -> Sketch097 [N_Axis]
  Refine = true
  Suppressed = false
  Type = 0
FEATURE [PartDesign::PolarPattern] PolarPattern018
  Angle = 360
  Axis = -> Sketch097 [N_Axis]
  BaseFeature = -> Pocket058
  Mode = 0
  Occurrences = 3
  Offset = 120
  Originals = -> [Pocket058]
  Placement = pos=(0,0,28) rot=(0,0,1;0rad)
  Refine = true
  Suppressed = false
  TransformMode = 0
FEATURE [Sketcher::SketchObject] Sketch098
  ArcFitTolerance = 1e-06
  AttachmentSupport = -> [PolarPattern018]
  FullyConstrained = false
  MakeInternals = false
  MapMode = 5
  Placement = pos=(0,0,28) rot=(0,0,1;0rad)
  sketch-geometry (6):
    g0: LineSegment StartX=-6.5 StartY=17.633 StartZ=0 EndX=-6.5 EndY=-8.00596 EndZ=0
    g1: LineSegment StartX=-4.13632 StartY=-10.3696 StartZ=0 EndX=-3.36368 EndY=-10.3696 EndZ=0
    g2: LineSegment StartX=-1 StartY=-8.00596 StartZ=0 EndX=-1 EndY=17.633 EndZ=0
    g3: LineSegment StartX=-1 StartY=17.633 StartZ=0 EndX=-6.5 EndY=17.633 EndZ=0
    g4: ArcOfCircle CenterX=-4.13632 CenterY=-8.00596 CenterZ=0 NormalX=0 NormalY=0 NormalZ=1 AngleXU=0 Radius=2.36368 StartAngle=3.14159 EndAngle=4.71239
    g5: ArcOfCircle CenterX=-3.36368 CenterY=-8.00596 CenterZ=0 NormalX=0 NormalY=0 NormalZ=1 AngleXU=0 Radius=2.36368 StartAngle=4.71239 EndAngle=6.28319
  constraints (17):
    c: Coincident(g2,g3)
    c: Coincident(g3,g0)
    c: Vertical(g0)
    c: Vertical(g2)
    c: Horizontal(g1)
    c: Horizontal(g3)
    c: DistanceX(g3,g3) = 5.5
    c: Distance(g-2,g2) = 1
    c: Horizontal(g4,g4)
    c: Horizontal(g4,g5)
    c: Horizontal(g5,g5)
    c: Vertical(g4,g4)
    c: Vertical(g5,g5)
    c: Coincident(g0,g4)
    c: Coincident(g1,g4)
    c: Coincident(g1,g5)
    c: Coincident(g2,g5)
FEATURE [PartDesign::Pocket] Pocket059
  BaseFeature = -> PolarPattern018
  Direction = (0,0,-1)
  Length = 40
  Length2 = 5
  Placement = pos=(0,0,28) rot=(0,0,1;0rad)
  Profile = -> Sketch098
  ReferenceAxis = -> Sketch098 [N_Axis]
  Refine = true
  Suppressed = false
  Type = 0
FEATURE [Sketcher::SketchObject] Sketch099
  ArcFitTolerance = 1e-06
  AttachmentSupport = -> [Pocket059]
  FullyConstrained = false
  MakeInternals = false
  MapMode = 5
  Placement = pos=(0,0,15) rot=(1,0,0;3.14159rad)
  sketch-geometry (4):
    g0: LineSegment StartX=-29.0592 StartY=5 StartZ=0 EndX=-29.0592 EndY=-5 EndZ=0
    g1: LineSegment StartX=-29.0592 StartY=-5 StartZ=0 EndX=0 EndY=-5 EndZ=0
    g2: LineSegment StartX=0 StartY=-5 StartZ=0 EndX=0 EndY=5 EndZ=0
    g3: LineSegment StartX=0 StartY=5 StartZ=0 EndX=-29.0592 EndY=5 EndZ=0
  constraints (11):
    c: Coincident(g0,g1)
    c: Coincident(g1,g2)
    c: Coincident(g2,g3)
    c: Coincident(g3,g0)
    c: Vertical(g0)
    c: Vertical(g2)
    c: Horizontal(g1)
    c: Horizontal(g3)
    c: PointOnObject(g1,g-2)
    c: Distance(g-1,g1) = 5
    c: Distance(g-1,g3) = 5
FEATURE [PartDesign::Pocket] Pocket060
  BaseFeature = -> Pocket059
  Direction = (0,0,1)
  Length = 8
  Length2 = 5
  Placement = pos=(0,0,28) rot=(0,0,1;0rad)
  Profile = -> Sketch099
  ReferenceAxis = -> Sketch099 [N_Axis]
  Refine = true
  Suppressed = false
  Type = 0
FEATURE [PartDesign::PolarPattern] PolarPattern
  Angle = 360
  Axis = -> Sketch099 [N_Axis]
  BaseFeature = -> Pocket060
  Mode = 0
  Occurrences = 3
  Offset = 120
  Originals = -> [Pocket060]
  Placement = pos=(0,0,28) rot=(0,0,1;0rad)
  Refine = true
  Suppressed = false
  TransformMode = 0
FEATURE [Sketcher::SketchObject] Sketch100
  ArcFitTolerance = 1e-06
  AttachmentSupport = -> [PolarPattern]
  FullyConstrained = false
  MakeInternals = false
  MapMode = 5
  Placement = pos=(0,0,28) rot=(0,0,1;0rad)
  sketch-geometry (4):
    g0: LineSegment StartX=-6 StartY=27.3621 StartZ=0 EndX=-27.2717 EndY=27.3621 EndZ=0
    g1: LineSegment StartX=-27.2717 StartY=27.3621 StartZ=0 EndX=-27.2717 EndY=-3 EndZ=0
    g2: LineSegment StartX=-27.2717 StartY=-3 StartZ=0 EndX=-6 EndY=-3 EndZ=0
    g3: LineSegment StartX=-6 StartY=-3 StartZ=0 EndX=-6 EndY=27.3621 EndZ=0
  constraints (10):
    c: Coincident(g0,g1)
    c: Coincident(g1,g2)
    c: Coincident(g2,g3)
    c: Coincident(g3,g0)
    c: Horizontal(g0)
    c: Horizontal(g2)
    c: Vertical(g1)
    c: Vertical(g3)
    c: Distance(g-2,g3) = 6
    c: Distance(g-1,g2) = 3
FEATURE [PartDesign::Pocket] Pocket061
  BaseFeature = -> PolarPattern
  Direction = (0,0,-1)
  Length = 8
  Length2 = 5
  Placement = pos=(0,0,28) rot=(0,0,1;0rad)
  Profile = -> Sketch100
  ReferenceAxis = -> Sketch100 [N_Axis]
  Refine = true
  Suppressed = false
  Type = 0
FEATURE [Sketcher::SketchObject] Sketch101
  ArcFitTolerance = 1e-06
  AttachmentSupport = -> [Pocket061]
  FullyConstrained = false
  MakeInternals = false
  MapMode = 5
  Placement = pos=(-1,0,28) rot=(0.57735,-0.57735,-0.57735;2.0944rad)
  sketch-geometry (4):
    g0: ArcOfCircle CenterX=-7 CenterY=1 CenterZ=0 NormalX=0 NormalY=0 NormalZ=1 AngleXU=0 Radius=8 StartAngle=3.71843 EndAngle=5.70367
    g1: LineSegment StartX=-18.8256 StartY=0 StartZ=0 EndX=-13.7055 EndY=-3.36301 EndZ=0
    g2: LineSegment StartX=4.85375 StartY=0 StartZ=0 EndX=-0.306155 EndY=-3.38092 EndZ=0
    g3: LineSegment StartX=-18.8256 StartY=0 StartZ=0 EndX=4.85375 EndY=0 EndZ=0
  constraints (9):
    c: Distance(g0,g-1) = 1
    c: DistanceX(g0,g-1) = 7
    c: Diameter(g0) = 16
    c: Coincident(g3,g1)
    c: Coincident(g3,g2)
    c: Coincident(g0,g2)
    c: Coincident(g1,g0)
    c: Horizontal(g3)
    c: Horizontal(g2,g-1)
FEATURE [PartDesign::Pocket] Pocket062
  BaseFeature = -> Pocket061
  Direction = (1,0,0)
  Length = 5
  Length2 = 5
  Placement = pos=(0,0,28) rot=(0,0,1;0rad)
  Profile = -> Sketch101
  ReferenceAxis = -> Sketch101 [N_Axis]
  Refine = true
  Suppressed = false
  Type = 0
FEATURE [Sketcher::SketchObject] Sketch102
  ArcFitTolerance = 1e-06
  AttachmentSupport = -> [Pocket062]
  FullyConstrained = true
  MakeInternals = false
  MapMode = 5
  Placement = pos=(-1,0,28) rot=(0.57735,-0.57735,-0.57735;2.0944rad)
  sketch-geometry (1):
    g0: Circle CenterX=-7 CenterY=1 CenterZ=0 NormalX=0 NormalY=0 NormalZ=1 AngleXU=0 Radius=8
  constraints (3):
    c: Diameter(g0) = 16
    c: Distance(g0,g-1) = 1
    c: DistanceX(g0,g-1) = 7
FEATURE [PartDesign::Pocket] Pocket063
  BaseFeature = -> Pocket062
  Direction = (1,0,0)
  Length = 5
  Length2 = 5
  Placement = pos=(0,0,28) rot=(0,0,1;0rad)
  Profile = -> Sketch102
  ReferenceAxis = -> Sketch102 [N_Axis]
  Refine = true
  Suppressed = false
  Type = 1
FEATURE [Sketcher::SketchObject] Sketch103
  ArcFitTolerance = 1e-06
  AttachmentSupport = -> [Pocket063]
  ExternalGeometry = -> [Pocket063]
  FullyConstrained = true
  MakeInternals = false
  MapMode = 5
  Placement = pos=(4,0,28) rot=(0.57735,-0.57735,-0.57735;2.0944rad)
  sketch-geometry (8):
    g0: LineSegment StartX=-14.9373 StartY=6e-16 StartZ=0 EndX=-14.9373 EndY=6 EndZ=0
    g1: LineSegment StartX=-14.9373 StartY=6 StartZ=0 EndX=-19.9373 EndY=3 EndZ=0
    g2: LineSegment StartX=-14.9373 StartY=6e-16 StartZ=0 EndX=-19.9373 EndY=0 EndZ=0
    g3: LineSegment StartX=-19.9373 StartY=3 StartZ=0 EndX=-19.9373 EndY=0 EndZ=0
    g4: LineSegment StartX=0.937254 StartY=-2.4e-15 StartZ=0 EndX=0.937254 EndY=6 EndZ=0
    g5: LineSegment StartX=0.937254 StartY=-2.4e-15 StartZ=0 EndX=5.93725 EndY=0 EndZ=0
    g6: LineSegment StartX=5.93725 StartY=0 StartZ=0 EndX=5.93725 EndY=3 EndZ=0
    g7: LineSegment StartX=0.937254 StartY=6 StartZ=0 EndX=5.93725 EndY=3 EndZ=0
  constraints (22):
    c: Vertical(g0)
    c: Coincident(g0,g-3)
    c: Coincident(g1,g0)
    c: Coincident(g2,g0)
    c: PointOnObject(g2,g-1)
    c: Coincident(g3,g1)
    c: Coincident(g3,g2)
    c: Vertical(g3)
    c: Distance(g2,g2) = 5
    c: Distance(g3,g3) = 3
    c: Distance(g0,g0) = 6
    c: Distance(g4) = 6
    c: Coincident(g4,g-4)
    c: Vertical(g4)
    c: Distance(g5) = 5
    c: Coincident(g5,g4)
    c: PointOnObject(g5,g-1)
    c: Distance(g6) = 3
    c: Coincident(g6,g5)
    c: Vertical(g6)
    c: Coincident(g7,g4)
    c: Coincident(g7,g6)
FEATURE [PartDesign::Pad] Pad014
  BaseFeature = -> Pocket063
  Direction = (-1,0,0)
  Length = 7
  Length2 = 10
  Placement = pos=(0,0,28) rot=(0,0,1;0rad)
  Profile = -> Sketch103
  ReferenceAxis = -> Sketch103 [N_Axis]
  Refine = true
  Reversed = true
  Suppressed = false
  Type = 0
FEATURE [Sketcher::SketchObject] Sketch104
  ArcFitTolerance = 1e-06
  AttachmentSupport = -> [Pad014]
  FullyConstrained = true
  MakeInternals = false
  MapMode = 5
  Placement = pos=(4,0,28) rot=(0.57735,-0.57735,-0.57735;2.0944rad)
  sketch-geometry (2):
    g0: Circle CenterX=3 CenterY=1.2 CenterZ=0 NormalX=0 NormalY=0 NormalZ=1 AngleXU=0 Radius=1.5
    g1: Circle CenterX=-17 CenterY=1.2 CenterZ=0 NormalX=0 NormalY=0 NormalZ=1 AngleXU=0 Radius=1.5
  constraints (6):
    c: Diameter(g0) = 3
    c: DistanceX(g-1,g0) = 3
    c: Distance(g0,g-1) = 1.2
    c: Diameter(g1) = 3
    c: Distance(g1,g-1) = 1.2
    c: DistanceX(g1,g-1) = 17
FEATURE [PartDesign::Pocket] Pocket064
  BaseFeature = -> Pad014
  Direction = (1,0,0)
  Length = 5
  Length2 = 5
  Placement = pos=(0,0,28) rot=(0,0,1;0rad)
  Profile = -> Sketch104
  ReferenceAxis = -> Sketch104 [N_Axis]
  Refine = true
  Suppressed = false
  Type = 0
FEATURE [Sketcher::SketchObject] Sketch105
  ArcFitTolerance = 1e-06
  AttachmentSupport = -> [Pocket064]
  FullyConstrained = false
  MakeInternals = false
  MapMode = 5
  Placement = pos=(0,-3,28) rot=(0,0.707107,0.707107;3.14159rad)
  sketch-geometry (2):
    g0: Circle CenterX=11.6455 CenterY=-2.2 CenterZ=0 NormalX=0 NormalY=0 NormalZ=1 AngleXU=0 Radius=1.5
    g1: Circle CenterX=18.1455 CenterY=-2.2 CenterZ=0 NormalX=0 NormalY=0 NormalZ=1 AngleXU=0 Radius=1.5
  constraints (5):
    c: Diameter(g0) = 3
    c: Diameter(g1) = 3
    c: Horizontal(g1,g0)
    c: DistanceY(g1,g-1) = 2.2
    c: DistanceX(g0,g1) = 6.5
FEATURE [PartDesign::Pocket] Pocket065
  BaseFeature = -> Pocket064
  Direction = (0,-1,2e-16)
  Length = 6
  Length2 = 5
  Placement = pos=(0,0,28) rot=(0,0,1;0rad)
  Profile = -> Sketch105
  ReferenceAxis = -> Sketch105 [N_Axis]
  Refine = true
  Suppressed = false
  Type = 0
FEATURE [Sketcher::SketchObject] Sketch113
  ArcFitTolerance = 1e-06
  AttachmentSupport = -> [Pocket065]
  FullyConstrained = true
  MakeInternals = false
  MapMode = 5
  Placement = pos=(0,0,28) rot=(0,0,1;0rad)
  sketch-geometry (3):
    g0: Circle CenterX=-15 CenterY=-8.5 CenterZ=0 NormalX=0 NormalY=0 NormalZ=1 AngleXU=0 Radius=2
    g1: Circle CenterX=15 CenterY=18 CenterZ=0 NormalX=0 NormalY=0 NormalZ=1 AngleXU=0 Radius=2
    g2: Circle CenterX=15 CenterY=-18 CenterZ=0 NormalX=0 NormalY=0 NormalZ=1 AngleXU=0 Radius=2
  constraints (9):
    c: Diameter(g0) = 4
    c: DistanceY(g0,g-1) = 8.5
    c: DistanceX(g0,g-1) = 15
    c: Diameter(g1) = 4
    c: DistanceX(g-1,g1) = 15
    c: DistanceY(g-1,g1) = 18
    c: Diameter(g2) = 4
    c: DistanceY(g2,g-1) = 18
    c: DistanceX(g-1,g2) = 15
FEATURE [PartDesign::Pocket] Pocket073
  BaseFeature = -> Pocket065
  Direction = (0,0,-1)
  Length = 10
  Length2 = 5
  Placement = pos=(0,0,28) rot=(0,0,1;0rad)
  Profile = -> Sketch113
  ReferenceAxis = -> Sketch113 [N_Axis]
  Refine = true
  Suppressed = false
  Type = 0
FEATURE [PartDesign::Body] Body012  label="GripperHolderMiddle002"
  AllowCompound = false
  Group = -> [Sketch092,Sketch093,AdditiveLoft007,Sketch095,Pad013,PolarPattern016,Sketch096,Pocket057,PolarPattern017,Sketch097,Pocket058,PolarPattern018,Sketch098,Pocket059,Sketch099,Pocket060,PolarPattern,Sketch100,Pocket061,Sketch101,Pocket062,Sketch102,Pocket063,Sketch103,Pad014,Sketch104,Pocket064,Sketch105,Pocket065,Sketch113,Pocket073]
  Origin = -> Origin012
  Placement = pos=(0,0,-28) rot=(0,0,1;0rad)
  Tip = -> Pocket073
COMPONENT P5 — geometry summary ("Finger001"; no construction recipe available for this part):
  bounding box: 97.6 x 18.3 x 15.7 mm
  tessellated surface: 4,476 triangles
  volume: 3560 mm^3 (13% of its bounding box)
COMPONENT P6 — geometry summary ("Finger"; no construction recipe available for this part):
  bounding box: 97.6 x 18.5 x 14.0 mm
  tessellated surface: 4,476 triangles
  volume: 3560 mm^3 (14% of its bounding box)
COMPONENT P7 — geometry summary ("Finger002"; no construction recipe available for this part):
  bounding box: 97.6 x 18.3 x 15.7 mm
  tessellated surface: 4,476 triangles
  volume: 3560 mm^3 (13% of its bounding box)
COMPONENT P8 — recipe-attached ("GripperMainShaft", modeled in this document).
Construction recipe (the document's own serialized feature program — sketch geometry with constraints, then the solid features built on it; lengths are millimeters unless a unit is written):

FEATURE [Sketcher::SketchObject] Sketch
  ArcFitTolerance = 1e-06
  AttachmentSupport = -> [XY_Plane]
  FullyConstrained = true
  MakeInternals = false
  MapMode = 5
  expr: Constraints[7] = <<Spreadsheet>>.GripperWidth / 2
  sketch-geometry (4):
    g0: ArcOfCircle CenterX=0 CenterY=0 CenterZ=0 NormalX=0 NormalY=0 NormalZ=1 AngleXU=0 Radius=22 StartAngle=1.5708 EndAngle=4.71239
    g1: ArcOfCircle CenterX=10 CenterY=-1.3e-15 CenterZ=0 NormalX=0 NormalY=0 NormalZ=1 AngleXU=0 Radius=22 StartAngle=4.71239 EndAngle=7.85398
    g2: LineSegment StartX=-3.5e-15 StartY=22 StartZ=0 EndX=10 EndY=22 EndZ=0
    g3: LineSegment StartX=-4e-15 StartY=-22 StartZ=0 EndX=10 EndY=-22 EndZ=0
  constraints (9):
    c: Tangent(g0,g2) = 1.5708
    c: Tangent(g0,g3) = -1.5708
    c: Tangent(g1,g2) = 1.5708
    c: Tangent(g1,g3) = -1.5708
    c: Equal(g0,g1)
    c: Horizontal(g3)
    c: Distance(g0,g1) = 10
    c: Radius(g0) = 22
    c: Coincident(g0,g-1)
FEATURE [PartDesign::Pad] Pad
  Direction = (0,0,1)
  Length = 15
  Length2 = 10
  Profile = -> Sketch
  ReferenceAxis = -> Sketch [N_Axis]
  Refine = true
  Reversed = true
  Suppressed = false
  Type = 0
FEATURE [Sketcher::SketchObject] Sketch001
  ArcFitTolerance = 1e-06
  AttachmentSupport = -> [Pad]
  FullyConstrained = true
  MakeInternals = false
  MapMode = 5
  Placement = pos=(0,-22,0) rot=(1,0,0;1.5708rad)
  sketch-geometry (4):
    g0: ArcOfCircle CenterX=0 CenterY=0 CenterZ=0 NormalX=0 NormalY=0 NormalZ=1 AngleXU=0 Radius=8 StartAngle=3.14159 EndAngle=6.28319
    g1: ArcOfCircle CenterX=-4e-16 CenterY=18 CenterZ=0 NormalX=0 NormalY=0 NormalZ=1 AngleXU=0 Radius=8 StartAngle=4.3e-15 EndAngle=3.14159
    g2: LineSegment StartX=-8 StartY=-6.634e-13 StartZ=0 EndX=-8 EndY=18 EndZ=0
    g3: LineSegment StartX=8 StartY=-3.004e-13 StartZ=0 EndX=8 EndY=18 EndZ=0
  constraints (9):
    c: Tangent(g0,g2) = 1.5708
    c: Tangent(g0,g3) = -1.5708
    c: Tangent(g1,g2) = 1.5708
    c: Tangent(g1,g3) = -1.5708
    c: Equal(g0,g1)
    c: Vertical(g3)
    c: DistanceY(g0,g1) = 18
    c: Radius(g1) = 8
    c: Coincident(g0,g-1)
FEATURE [PartDesign::Pocket] Pocket
  BaseFeature = -> Pad
  Direction = (0,1,-2e-16)
  Length = 5
  Length2 = 5
  Profile = -> Sketch001
  ReferenceAxis = -> Sketch001 [N_Axis]
  Refine = true
  Suppressed = false
  Type = 0
FEATURE [Sketcher::SketchObject] Sketch002
  ArcFitTolerance = 1e-06
  AttachmentSupport = -> [Pocket]
  FullyConstrained = true
  MakeInternals = false
  MapMode = 5
  Placement = pos=(0,-17,0) rot=(1,0,0;1.5708rad)
  expr: Constraints[6] = <<Spreadsheet>>.UpperBearingHole
  expr: Constraints[7] = <<Spreadsheet>>.FirstToSecondHoleSpace
  sketch-geometry (5):
    g0: LineSegment StartX=-8 StartY=0 StartZ=0 EndX=8 EndY=0 EndZ=0
    g1: LineSegment StartX=8 StartY=0 StartZ=0 EndX=6 EndY=15 EndZ=0
    g2: LineSegment StartX=-6 StartY=15 StartZ=0 EndX=-8 EndY=0 EndZ=0
    g3: ArcOfCircle CenterX=-1e-16 CenterY=13 CenterZ=0 NormalX=0 NormalY=0 NormalZ=1 AngleXU=0 Radius=6.32456 StartAngle=0.321751 EndAngle=2.81984
    g4: Circle CenterX=-1e-16 CenterY=13 CenterZ=0 NormalX=0 NormalY=0 NormalZ=1 AngleXU=0 Radius=4
  constraints (15):
    c: Coincident(g0,g1)
    c: Coincident(g2,g0)
    c: Horizontal(g0)
    c: Coincident(g3,g2)
    c: Coincident(g3,g1)
    c: Coincident(g4,g3)
    c: Diameter(g4) = 8
    c: Distance(g3,g0) = 13
    c: Distance(g2,g-2) = 6
    c: Distance(g1,g-2) = 6
    c: Horizontal(g1,g2)
    c: Distance(g0,g-2) = 8
    c: Distance(g0,g-2) = 8
    c: Distance(g2,g0) = 15
    c: Horizontal(g0,g-1)
FEATURE [PartDesign::Pad] Pad001
  BaseFeature = -> Pocket
  Direction = (0,-1,2e-16)
  Length = 5
  Length2 = 10
  Profile = -> Sketch002
  ReferenceAxis = -> Sketch002 [N_Axis]
  Refine = true
  Reversed = true
  Suppressed = false
  Type = 0
FEATURE [Sketcher::SketchObject] Sketch003
  ArcFitTolerance = 1e-06
  AttachmentSupport = -> [Pad001]
  FullyConstrained = true
  MakeInternals = false
  MapMode = 5
  Placement = pos=(0,-17,0) rot=(1,0,0;1.5708rad)
  expr: Constraints[0] = <<Spreadsheet>>.GripperLowerHoleDiameter
  sketch-geometry (1):
    g0: Circle CenterX=0 CenterY=0 CenterZ=0 NormalX=0 NormalY=0 NormalZ=1 AngleXU=0 Radius=2.5
  constraints (2):
    c: Diameter(g0) = 5
    c: Coincident(g0,g-1)
FEATURE [PartDesign::Pad] Pad002
  BaseFeature = -> Pad001
  Direction = (0,-1,2e-16)
  Length = 6
  Length2 = 10
  Profile = -> Sketch003
  ReferenceAxis = -> Sketch003 [N_Axis]
  Refine = true
  Suppressed = false
  Type = 0
FEATURE [Sketcher::SketchObject] Sketch004
  ArcFitTolerance = 1e-06
  AttachmentSupport = -> [Pad002]
  FullyConstrained = true
  MakeInternals = false
  MapMode = 5
  expr: Constraints[0] = <<Spreadsheet>>.GripperWidth / 2
  sketch-geometry (3):
    g0: ArcOfCircle CenterX=0 CenterY=0 CenterZ=0 NormalX=0 NormalY=0 NormalZ=1 AngleXU=0 Radius=22 StartAngle=3.14159 EndAngle=4.34022
    g1: LineSegment StartX=-8 StartY=2.7e-15 StartZ=0 EndX=-22 EndY=2.7e-15 EndZ=0
    g2: LineSegment StartX=-8 StartY=2.7e-15 StartZ=0 EndX=-8 EndY=-20.4939 EndZ=0
  constraints (9):
    c: Radius(g0) = 22
    c: Coincident(g0,g-1)
    c: PointOnObject(g1,g-1)
    c: Coincident(g1,g0)
    c: Horizontal(g1)
    c: Coincident(g2,g1)
    c: Coincident(g2,g0)
    c: Vertical(g2)
    c: Distance(g-2,g2) = 8
FEATURE [Sketcher::SketchObject] Sketch005
  ArcFitTolerance = 1e-06
  AttachmentOffset = pos=(0,0,15) rot=(0,0,1;0rad)
  AttachmentSupport = -> [Pad002]
  FullyConstrained = false
  MakeInternals = false
  MapMode = 5
  Placement = pos=(0,0,15) rot=(0,0,1;0rad)
  sketch-geometry (3):
    g0: ArcOfCircle CenterX=8.29499 CenterY=0 CenterZ=0 NormalX=0 NormalY=0 NormalZ=1 AngleXU=0 Radius=22.2114 StartAngle=3.14159 EndAngle=4.01321
    g1: LineSegment StartX=-6 StartY=-17 StartZ=0 EndX=-6 EndY=0 EndZ=0
    g2: LineSegment StartX=-13.9164 StartY=2.7e-15 StartZ=0 EndX=-6 EndY=0 EndZ=0
  constraints (9):
    c: PointOnObject(g0,g-1)
    c: PointOnObject(g0,g-1)
    c: Distance(g0,g-1) = 17
    c: Vertical(g1)
    c: Coincident(g1,g0)
    c: PointOnObject(g1,g-1)
    c: Coincident(g0,g2)
    c: Coincident(g1,g2)
    c: Distance(g-2,g1) = 6
FEATURE [PartDesign::AdditiveLoft] AdditiveLoft
  BaseFeature = -> Pad002
  Closed = false
  Profile = -> Sketch005
  Refine = true
  Ruled = false
  Sections = -> [Sketch004]
  Suppressed = false
FEATURE [Sketcher::SketchObject] Sketch006
  ArcFitTolerance = 1e-06
  AttachmentSupport = -> [XY_Plane]
  FullyConstrained = false
  MakeInternals = false
  MapMode = 5
  sketch-geometry (4):
    g0: LineSegment StartX=-33.6421 StartY=0 StartZ=0 EndX=60.4928 EndY=0 EndZ=0
    g1: LineSegment StartX=60.4928 StartY=0 StartZ=0 EndX=60.4928 EndY=42.6124 EndZ=0
    g2: LineSegment StartX=60.4928 StartY=42.6124 StartZ=0 EndX=-33.6421 EndY=42.6124 EndZ=0
    g3: LineSegment StartX=-33.6421 StartY=42.6124 StartZ=0 EndX=-33.6421 EndY=0 EndZ=0
  constraints (9):
    c: Coincident(g0,g1)
    c: Coincident(g1,g2)
    c: Coincident(g2,g3)
    c: Coincident(g3,g0)
    c: Horizontal(g0)
    c: Horizontal(g2)
    c: Vertical(g1)
    c: Vertical(g3)
    c: PointOnObject(g0,g-1)
FEATURE [PartDesign::Pocket] Pocket001
  BaseFeature = -> AdditiveLoft
  Direction = (0,0,-1)
  Length = 5
  Length2 = 5
  Profile = -> Sketch006
  ReferenceAxis = -> Sketch006 [N_Axis]
  Refine = true
  Suppressed = false
  Type = 1
FEATURE [Sketcher::SketchObject] Sketch007
  ArcFitTolerance = 1e-06
  AttachmentSupport = -> [Pocket001]
  FullyConstrained = false
  MakeInternals = false
  MapMode = 5
  Placement = pos=(0,-22,0) rot=(1,0,0;1.5708rad)
  sketch-geometry (5):
    g0: LineSegment StartX=16.5479 StartY=15.5515 StartZ=0 EndX=45.6805 EndY=15.5515 EndZ=0
    g1: LineSegment StartX=16.5479 StartY=15.5515 StartZ=0 EndX=25.3255 EndY=6.77388 EndZ=0
    g2: LineSegment StartX=25.3255 StartY=6.77388 StartZ=0 EndX=25.3255 EndY=3.99498 EndZ=0
    g3: LineSegment StartX=25.3255 StartY=3.99498 StartZ=0 EndX=45.6805 EndY=3.99498 EndZ=0
    g4: LineSegment StartX=45.6805 StartY=15.5515 StartZ=0 EndX=45.6805 EndY=3.99498 EndZ=0
  constraints (10):
    c: Horizontal(g0)
    c: Angle(g-1,g1) = -0.785398
    c: Coincident(g1,g0)
    c: Vertical(g2)
    c: Coincident(g2,g1)
    c: Horizontal(g3)
    c: Coincident(g3,g2)
    c: Coincident(g4,g0)
    c: Coincident(g4,g3)
    c: Vertical(g4)
FEATURE [PartDesign::Pocket] Pocket002
  BaseFeature = -> Pocket001
  Direction = (0,1,-2e-16)
  Length = 20
  Length2 = 5
  Profile = -> Sketch007
  ReferenceAxis = -> Sketch007 [N_Axis]
  Refine = true
  Suppressed = false
  Type = 1
FEATURE [Sketcher::SketchObject] Sketch063
  ArcFitTolerance = 1e-06
  AttachmentSupport = -> [Pocket002]
  FullyConstrained = false
  MakeInternals = false
  MapMode = 5
  Placement = pos=(0,-22,0) rot=(1,0,0;1.5708rad)
  sketch-geometry (3):
    g0: LineSegment StartX=14 StartY=0 StartZ=0 EndX=40.2734 EndY=-26.2734 EndZ=0
    g1: LineSegment StartX=14 StartY=0 StartZ=0 EndX=40.2734 EndY=0 EndZ=0
    g2: LineSegment StartX=40.2734 StartY=0 StartZ=0 EndX=40.2734 EndY=-26.2734 EndZ=0
  constraints (8):
    c: Angle(g0,g-1) = 0.785398
    c: Horizontal(g0,g-1)
    c: DistanceX(g-1,g0) = 14
    c: Coincident(g1,g0)
    c: PointOnObject(g1,g-1)
    c: Coincident(g2,g1)
    c: Coincident(g2,g0)
    c: Vertical(g2)
FEATURE [PartDesign::Pocket] Pocket030
  BaseFeature = -> Pocket002
  Direction = (0,1,-2e-16)
  Length = 12
  Length2 = 5
  Profile = -> Sketch063
  ReferenceAxis = -> Sketch063 [N_Axis]
  Refine = true
  Suppressed = false
  Type = 1
FEATURE [PartDesign::Mirrored] Mirrored006
  BaseFeature = -> Pocket030
  MirrorPlane = -> XZ_Plane
  Originals = -> [Pocket030]
  Refine = true
  Suppressed = false
  TransformMode = 1
FEATURE [Sketcher::SketchObject] Sketch106
  ArcFitTolerance = 1e-06
  AttachmentSupport = -> [Mirrored006]
  FullyConstrained = false
  MakeInternals = false
  MapMode = 5
  Placement = pos=(0,3.4e-15,-15) rot=(1,0,0;3.14159rad)
  sketch-geometry (4):
    g0: LineSegment StartX=-10.6241 StartY=11.3884 StartZ=0 EndX=-10.6241 EndY=-14.7 EndZ=0
    g1: LineSegment StartX=-10.6241 StartY=-14.7 StartZ=0 EndX=12.7711 EndY=-14.7 EndZ=0
    g2: LineSegment StartX=12.7711 StartY=-14.7 StartZ=0 EndX=12.7711 EndY=11.3884 EndZ=0
    g3: LineSegment StartX=12.7711 StartY=11.3884 StartZ=0 EndX=-10.6241 EndY=11.3884 EndZ=0
  constraints (9):
    c: Coincident(g0,g1)
    c: Coincident(g1,g2)
    c: Coincident(g2,g3)
    c: Coincident(g3,g0)
    c: Vertical(g0)
    c: Vertical(g2)
    c: Horizontal(g1)
    c: Horizontal(g3)
    c: Distance(g-1,g1) = 14.7
FEATURE [PartDesign::Pocket] Pocket066
  BaseFeature = -> Mirrored006
  Direction = (0,0,1)
  Length = 12
  Length2 = 5
  Profile = -> Sketch106
  ReferenceAxis = -> Sketch106 [N_Axis]
  Refine = true
  Suppressed = false
  Type = 0
FEATURE [Sketcher::SketchObject] Sketch107
  ArcFitTolerance = 1e-06
  AttachmentSupport = -> [Pocket066]
  FullyConstrained = false
  MakeInternals = false
  MapMode = 5
  Placement = pos=(12.7711,0,0) rot=(0.57735,-0.57735,-0.57735;2.0944rad)
  sketch-geometry (4):
    g0: LineSegment StartX=-14.7 StartY=-3 StartZ=0 EndX=-14.7 EndY=-21.6699 EndZ=0
    g1: LineSegment StartX=-14.7 StartY=-21.6699 StartZ=0 EndX=6.51936 EndY=-21.6699 EndZ=0
    g2: LineSegment StartX=6.51936 StartY=-21.6699 StartZ=0 EndX=6.51936 EndY=-3 EndZ=0
    g3: LineSegment StartX=6.51936 StartY=-3 StartZ=0 EndX=-14.7 EndY=-3 EndZ=0
  constraints (9):
    c: Coincident(g0,g1)
    c: Coincident(g1,g2)
    c: Coincident(g2,g3)
    c: Coincident(g3,g0)
    c: Vertical(g0)
    c: Vertical(g2)
    c: Horizontal(g1)
    c: Horizontal(g3)
    c: Distance(g-2,g0) = 14.7
FEATURE [PartDesign::Pocket] Pocket067
  BaseFeature = -> Pocket066
  Direction = (1,0,0)
  Length = 25
  Length2 = 5
  Profile = -> Sketch107
  ReferenceAxis = -> Sketch107 [N_Axis]
  Refine = true
  Suppressed = false
  Type = 1
FEATURE [Sketcher::SketchObject] Sketch108
  ArcFitTolerance = 1e-06
  AttachmentSupport = -> [YZ_Plane]
  FullyConstrained = false
  MakeInternals = false
  MapMode = 5
  Placement = pos=(0,0,0) rot=(0.57735,0.57735,0.57735;2.0944rad)
  sketch-geometry (4):
    g0: LineSegment StartX=14.8357 StartY=-7.40568 StartZ=0 EndX=20.3815 EndY=-10.7555 EndZ=0
    g1: LineSegment StartX=20.3815 StartY=-10.7555 StartZ=0 EndX=20.3815 EndY=-15.57 EndZ=0
    g2: LineSegment StartX=14.8357 StartY=-7.40568 StartZ=0 EndX=14.8357 EndY=-15.57 EndZ=0
    g3: LineSegment StartX=14.8357 StartY=-15.57 StartZ=0 EndX=20.3815 EndY=-15.57 EndZ=0
  constraints (7):
    c: Coincident(g0,g1)
    c: Vertical(g1)
    c: Coincident(g2,g0)
    c: Vertical(g2)
    c: Coincident(g3,g2)
    c: Coincident(g3,g1)
    c: Horizontal(g3)
FEATURE [PartDesign::Pocket] Pocket068
  BaseFeature = -> Pocket067
  Direction = (-1,0,0)
  Length = 12
  Length2 = 5
  Profile = -> Sketch108
  ReferenceAxis = -> Sketch108 [N_Axis]
  Refine = true
  Reversed = true
  Suppressed = false
  Type = 0
FEATURE [Sketcher::SketchObject] Sketch111
  ArcFitTolerance = 1e-06
  AttachmentSupport = -> [Pocket068]
  FullyConstrained = true
  MakeInternals = false
  MapMode = 5
  Placement = pos=(0,3.4e-15,-15) rot=(1,0,0;3.14159rad)
  sketch-geometry (4):
    g0: Circle CenterX=15 CenterY=-18 CenterZ=0 NormalX=0 NormalY=0 NormalZ=1 AngleXU=0 Radius=1.5
    g1: Circle CenterX=15 CenterY=18 CenterZ=0 NormalX=0 NormalY=0 NormalZ=1 AngleXU=0 Radius=1.5
    g2: Circle CenterX=-15 CenterY=8.5 CenterZ=0 NormalX=0 NormalY=0 NormalZ=1 AngleXU=0 Radius=1.5
    g3: Circle CenterX=-15 CenterY=-8.5 CenterZ=0 NormalX=0 NormalY=0 NormalZ=1 AngleXU=0 Radius=1.5
  constraints (12):
    c: Diameter(g0) = 3
    c: DistanceY(g0,g-1) = 18
    c: DistanceX(g-1,g0) = 15
    c: Diameter(g1) = 3
    c: DistanceY(g-1,g1) = 18
    c: DistanceX(g-1,g1) = 15
    c: Diameter(g2) = 3
    c: Diameter(g3) = 3
    c: DistanceX(g2,g-1) = 15
    c: DistanceX(g3,g-1) = 15
    c: DistanceY(g3,g-1) = 8.5
    c: DistanceY(g-1,g2) = 8.5
FEATURE [Sketcher::SketchObject] Sketch109
  ArcFitTolerance = 1e-06
  AttachmentSupport = -> [Pocket068]
  ExternalGeometry = -> [Pocket068]
  FullyConstrained = false
  MakeInternals = false
  MapMode = 5
  Placement = pos=(0,0,-1.74e-14) rot=(0,0,1;0rad)
  sketch-geometry (4):
    g0: LineSegment StartX=-8 StartY=10 StartZ=0 EndX=-8 EndY=-6.51936 EndZ=0
    g1: LineSegment StartX=-8 StartY=-6.51936 StartZ=0 EndX=23.7244 EndY=-6.51936 EndZ=0
    g2: LineSegment StartX=23.7244 StartY=-6.51936 StartZ=0 EndX=23.7244 EndY=10 EndZ=0
    g3: LineSegment StartX=23.7244 StartY=10 StartZ=0 EndX=-8 EndY=10 EndZ=0
  constraints (11):
    c: Coincident(g0,g1)
    c: Coincident(g1,g2)
    c: Coincident(g2,g3)
    c: Coincident(g3,g0)
    c: Vertical(g0)
    c: Vertical(g2)
    c: Horizontal(g1)
    c: Horizontal(g3)
    c: Vertical(g0,g-3)
    c: Horizontal(g1,g-4)
    c: Horizontal(g-5,g2)
FEATURE [PartDesign::Pocket] Pocket069
  BaseFeature = -> Pocket068
  Direction = (0,0,-1)
  Length = 5
  Length2 = 5
  Profile = -> Sketch109
  ReferenceAxis = -> Sketch109 [N_Axis]
  Refine = true
  Suppressed = false
  Type = 0
FEATURE [Sketcher::SketchObject] Sketch110
  ArcFitTolerance = 1e-06
  AttachmentSupport = -> [Pocket069]
  ExternalGeometry = -> [Pocket069]
  FullyConstrained = false
  MakeInternals = false
  MapMode = 5
  Placement = pos=(0,0,-1.74e-14) rot=(0,0,1;0rad)
  sketch-geometry (4):
    g0: LineSegment StartX=-8 StartY=-11.3884 StartZ=0 EndX=-8 EndY=-1.01469 EndZ=0
    g1: LineSegment StartX=-8 StartY=-1.01469 StartZ=0 EndX=0 EndY=-1.01469 EndZ=0
    g2: LineSegment StartX=0 StartY=-1.01469 StartZ=0 EndX=0 EndY=-11.3884 EndZ=0
    g3: LineSegment StartX=0 StartY=-11.3884 StartZ=0 EndX=-8 EndY=-11.3884 EndZ=0
  constraints (11):
    c: Coincident(g0,g1)
    c: Coincident(g1,g2)
    c: Coincident(g2,g3)
    c: Coincident(g3,g0)
    c: Vertical(g0)
    c: Vertical(g2)
    c: Horizontal(g1)
    c: Horizontal(g3)
    c: Vertical(g0,g-3)
    c: Horizontal(g0,g-4)
    c: Vertical(g1,g-1)
FEATURE [PartDesign::Pocket] Pocket070
  BaseFeature = -> Pocket069
  Direction = (0,0,-1)
  Length = 5
  Length2 = 5
  Profile = -> Sketch110
  ReferenceAxis = -> Sketch110 [N_Axis]
  Refine = true
  Suppressed = false
  Type = 0
FEATURE [PartDesign::Pocket] Pocket071
  BaseFeature = -> Pocket070
  Direction = (0,0,1)
  Length = 5
  Length2 = 5
  Profile = -> Sketch111
  ReferenceAxis = -> Sketch111 [N_Axis]
  Refine = true
  Suppressed = false
  Type = 1
FEATURE [Sketcher::SketchObject] Sketch112
  ArcFitTolerance = 1e-06
  AttachmentOffset = pos=(0,0,-2) rot=(0,0,1;0rad)
  AttachmentSupport = -> [Pocket071]
  ExternalGeometry = -> [Pocket071]
  FullyConstrained = true
  MakeInternals = false
  MapMode = 5
  Placement = pos=(0,3.4e-15,-13) rot=(1,0,0;3.14159rad)
  sketch-geometry (4):
    g0: Circle CenterX=15 CenterY=18 CenterZ=0 NormalX=0 NormalY=0 NormalZ=1 AngleXU=0 Radius=3
    g1: Circle CenterX=15 CenterY=-18 CenterZ=0 NormalX=0 NormalY=0 NormalZ=1 AngleXU=0 Radius=3
    g2: Circle CenterX=-15 CenterY=-8.5 CenterZ=0 NormalX=0 NormalY=0 NormalZ=1 AngleXU=0 Radius=3
    g3: Circle CenterX=-15 CenterY=8.5 CenterZ=0 NormalX=0 NormalY=0 NormalZ=1 AngleXU=0 Radius=3
  constraints (8):
    c: Diameter(g0) = 6
    c: Coincident(g0,g-4)
    c: Diameter(g1) = 6
    c: Coincident(g1,g-5)
    c: Diameter(g2) = 6
    c: Coincident(g2,g-6)
    c: Diameter(g3) = 6
    c: Coincident(g3,g-3)
FEATURE [PartDesign::Pocket] Pocket072
  BaseFeature = -> Pocket071
  Direction = (0,0,1)
  Length = 5
  Length2 = 5
  Profile = -> Sketch112
  ReferenceAxis = -> Sketch112 [N_Axis]
  Refine = true
  Suppressed = false
  Type = 1
FEATURE [PartDesign::Chamfer] Chamfer001
  Angle = 45
  Base = -> Pocket072 [Edge108]
  BaseFeature = -> Pocket072
  ChamferType = 0
  FlipDirection = false
  Refine = true
  Size = 3
  Size2 = 1
  SupportTransform = false
  Suppressed = false
  UseAllEdges = false
FEATURE [Sketcher::SketchObject] Sketch114
  ArcFitTolerance = 1e-06
  AttachmentSupport = -> [Chamfer001]
  FullyConstrained = false
  MakeInternals = false
  MapMode = 5
  Placement = pos=(0,3.4e-15,-15) rot=(1,0,0;3.14159rad)
  sketch-geometry (4):
    g0: LineSegment StartX=-25.3466 StartY=3 StartZ=0 EndX=-25.3466 EndY=-3 EndZ=0
    g1: LineSegment StartX=-25.3466 StartY=-3 StartZ=0 EndX=-6.65232 EndY=-3 EndZ=0
    g2: LineSegment StartX=-6.65232 StartY=-3 StartZ=0 EndX=-6.65232 EndY=3 EndZ=0
    g3: LineSegment StartX=-6.65232 StartY=3 StartZ=0 EndX=-25.3466 EndY=3 EndZ=0
  constraints (10):
    c: Coincident(g0,g1)
    c: Coincident(g1,g2)
    c: Coincident(g2,g3)
    c: Coincident(g3,g0)
    c: Vertical(g0)
    c: Vertical(g2)
    c: Horizontal(g1)
    c: Horizontal(g3)
    c: Distance(g-1,g3) = 3
    c: Distance(g-1,g1) = 3
FEATURE [PartDesign::Pocket] Pocket074
  BaseFeature = -> Chamfer001
  Direction = (0,0,1)
  Length = 10
  Length2 = 5
  Profile = -> Sketch114
  ReferenceAxis = -> Sketch114 [N_Axis]
  Refine = true
  Suppressed = false
  Type = 0
FEATURE [Sketcher::SketchObject] Sketch117
  ArcFitTolerance = 1e-06
  AttachmentSupport = -> [Pocket074]
  FullyConstrained = true
  MakeInternals = false
  MapMode = 5
  Placement = pos=(-8,0,0) rot=(0.57735,0.57735,0.57735;2.0944rad)
  sketch-geometry (4):
    g0: LineSegment StartX=7 StartY=0 StartZ=0 EndX=7 EndY=8 EndZ=0
    g1: LineSegment StartX=7 StartY=8 StartZ=0 EndX=-7 EndY=8 EndZ=0
    g2: LineSegment StartX=-7 StartY=8 StartZ=0 EndX=-7 EndY=0 EndZ=0
    g3: LineSegment StartX=-7 StartY=0 StartZ=0 EndX=7 EndY=0 EndZ=0
  constraints (12):
    c: Coincident(g0,g1)
    c: Coincident(g1,g2)
    c: Coincident(g2,g3)
    c: Coincident(g3,g0)
    c: Vertical(g0)
    c: Vertical(g2)
    c: Horizontal(g1)
    c: Horizontal(g3)
    c: PointOnObject(g0,g-1)
    c: Distance(g-2,g2) = 7
    c: Distance(g-2,g0) = 7
    c: Distance(g-1,g1) = 8
FEATURE [PartDesign::Pocket] Pocket077
  BaseFeature = -> Pocket074
  Direction = (-1,0,0)
  Length = 5
  Length2 = 5
  Profile = -> Sketch117
  ReferenceAxis = -> Sketch117 [N_Axis]
  Refine = true
  Reversed = true
  Suppressed = false
  Type = 0
FEATURE [Sketcher::SketchObject] Sketch118
  ArcFitTolerance = 1e-06
  AttachmentSupport = -> [Pocket077]
  FullyConstrained = true
  MakeInternals = false
  MapMode = 5
  Placement = pos=(-8,0,0) rot=(0.57735,0.57735,0.57735;2.0944rad)
  sketch-geometry (2):
    g0: Circle CenterX=-3.25 CenterY=5.1 CenterZ=0 NormalX=0 NormalY=0 NormalZ=1 AngleXU=0 Radius=1.5
    g1: Circle CenterX=3.25 CenterY=5.1 CenterZ=0 NormalX=0 NormalY=0 NormalZ=1 AngleXU=0 Radius=1.5
  constraints (6):
    c: Diameter(g0) = 3
    c: Diameter(g1) = 3
    c: DistanceX(g0,g-1) = 3.25
    c: Distance(g1,g-2) = 3.25
    c: DistanceY(g-1,g0) = 5.1
    c: Horizontal(g1,g0)
FEATURE [PartDesign::Pocket] Pocket078
  BaseFeature = -> Pocket077
  Direction = (-1,0,0)
  Length = 5
  Length2 = 5
  Profile = -> Sketch118
  ReferenceAxis = -> Sketch118 [N_Axis]
  Refine = true
  Suppressed = false
  Type = 1
FEATURE [PartDesign::Body] Body  label="GripperHolder"
  AllowCompound = false
  Group = -> [Sketch,Pad,Sketch001,Pocket,Sketch002,Pad001,Sketch003,Pad002,Sketch004,Sketch005,AdditiveLoft,Sketch006,Pocket001,Sketch007,Pocket002,Sketch063,Pocket030,Mirrored006,Sketch106,Pocket066,Sketch107,Pocket067,Sketch108,Pocket068,Sketch109,Pocket069,Sketch110,Pocket070,Sketch111,Pocket071,Sketch112,Pocket072,Chamfer001,Sketch114,Pocket074,Sketch117,Pocket077,Sketch118,Pocket078]
  Origin = -> Origin
  Placement = pos=(0,0,15) rot=(0,0,1;0rad)
  Tip = -> Pocket078
COMPONENT P9 — geometry summary ("GM12-15BY001"; no construction recipe available for this part):
  bounding box: 32.0 x 24.0 x 15.0 mm
  tessellated surface: 15,100 triangles
  volume: 3996 mm^3 (35% of its bounding box)
COMPONENT P10 — geometry summary ("ChessPieces"; no construction recipe available for this part):
  bounding box: 55.0 x 27.5 x 25.0 mm
  tessellated surface: 140,842 triangles
  volume: 30978 mm^3 (82% of its bounding box)
PROVENANCE & LICENSES
A FreeCAD (.FCStd) document from a public repository crawl; recipes are the document's own serialized feature recipes (and, for linked parts, companion documents' recipes).
License: as declared in the source repository (recorded in the dataset sidecar).
